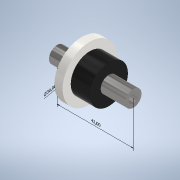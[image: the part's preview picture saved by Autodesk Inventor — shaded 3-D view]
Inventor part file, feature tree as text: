
AUTODESK INVENTOR PART (.ipt)
format: ipt  version: 2022.6 (Build 266554000, 554)  size: 179,712 bytes
history: native  units: mm
features: other x3, extrude x3, hole x1, mirror x1, plane x1
ambient origin geometry x8: Origin, YZ Plane, XZ Plane, XY Plane, X Axis, Y Axis, Z Axis, Center Point
bodies: Solid1 (feature_tree)
feature tree (9):
  other  "Annotations"
  extrude  "Extrusion1"  Depth=9.0mm
  hole  "Hole1"  [1 undecoded]
  mirror  "Mirror1"
  plane  "Work Plane2"
  extrude  "Extrusion2"  Depth=30.0mm
  extrude  "Extrusion3"  Depth=4.5mm TaperAngle=0.0deg
  other  "Linear Dimension 1"
  other  "Diameter Dimension 1"
note: 1 required parameter value undecoded (feature->parameter linkage not recoverable at this tier; creation-order binding heuristic only, values carry confidence <= 0.55)
